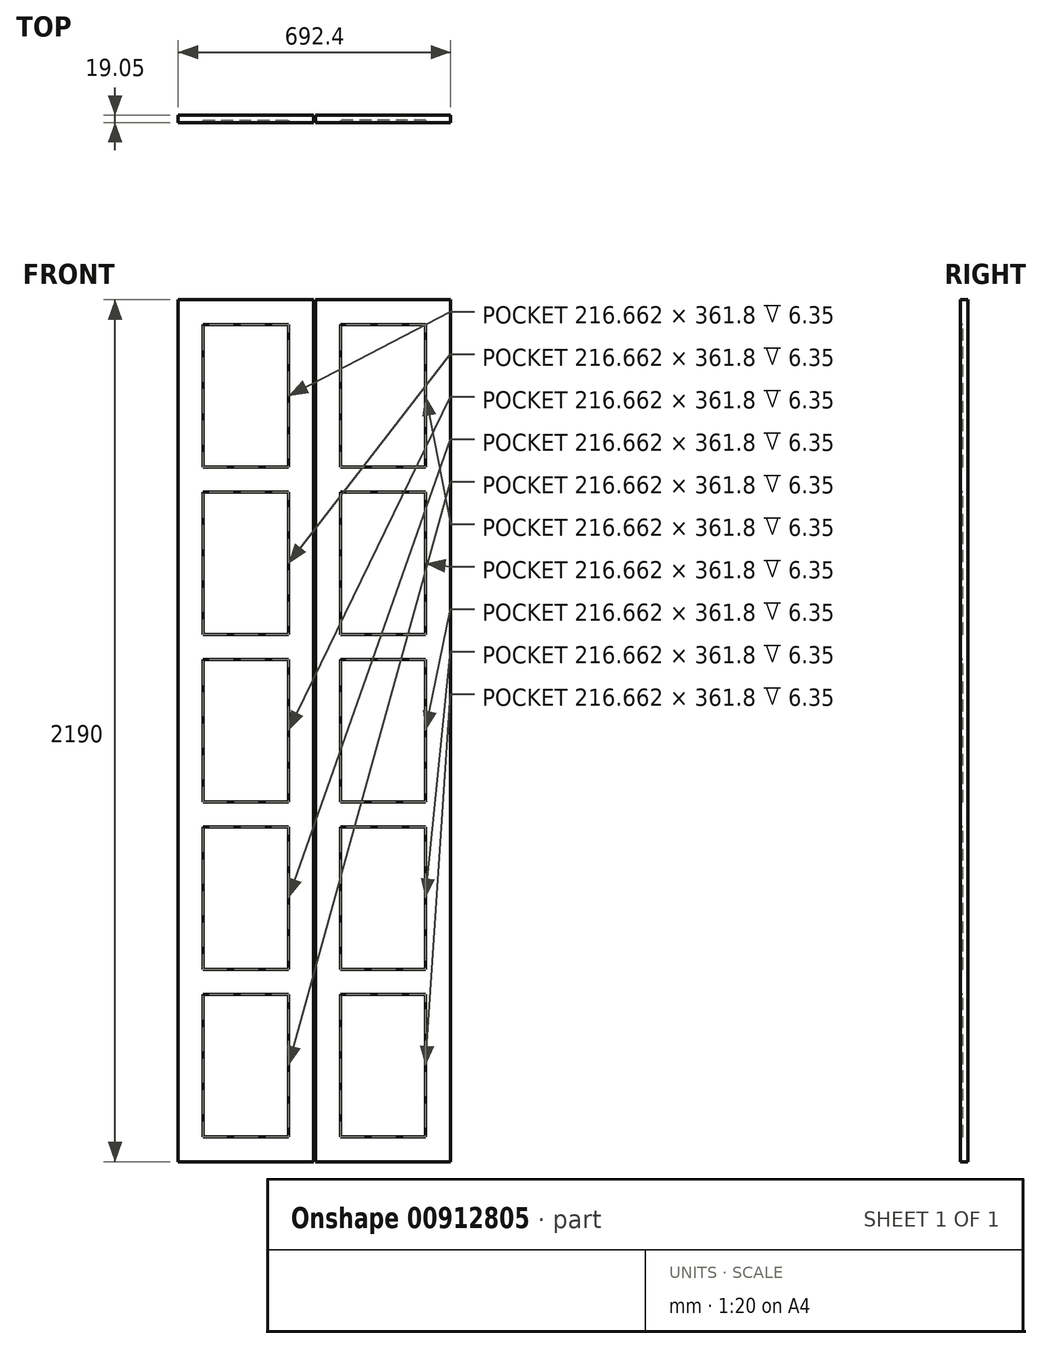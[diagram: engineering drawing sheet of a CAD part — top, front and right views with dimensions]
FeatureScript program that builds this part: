
annotation { "Feature Type Name" : "Feature", "Feature Type Description" : "" }
export const myFeature = defineFeature(function(context is Context, id is Id, definition is map)
    precondition{}
    {
        {
            var Q0;
            Q0=qCreatedBy(makeId("Front.planeOp"),FACE);
            var sketch = newSketch(context, id + "F0", { "sketchPlane" : qUnion([Q0])});
            skLineSegment(sketch, "E0.bottom", {"start": v(-336.55, 0) * mm, "end": v(336.55, 0) * mm, "construction": true});
            skLineSegment(sketch, "E0.top", {"start": v(-336.55, 2159) * mm, "end": v(336.55, 2159) * mm, "construction": true});
            skLineSegment(sketch, "E0.left", {"start": v(-336.55, 0) * mm, "end": v(-336.55, 2159) * mm, "construction": true});
            skLineSegment(sketch, "E0.right", {"start": v(336.55, 0) * mm, "end": v(336.55, 2159) * mm, "construction": true});
            skLineSegment(sketch, "E1.bottom", {"start": v(-336.55, 1814) * mm, "end": v(336.55, 1814) * mm, "construction": true});
            skLineSegment(sketch, "E1.top", {"start": v(-336.55, 1795) * mm, "end": v(336.55, 1795) * mm, "construction": true});
            skLineSegment(sketch, "E1.left", {"start": v(-336.55, 1814) * mm, "end": v(-336.55, 1795) * mm, "construction": true});
            skLineSegment(sketch, "E1.right", {"start": v(336.55, 1814) * mm, "end": v(336.55, 1795) * mm, "construction": true});
            skLineSegment(sketch, "E2.bottom", {"start": v(-336.55, 1450) * mm, "end": v(336.55, 1450) * mm, "construction": true});
            skLineSegment(sketch, "E2.top", {"start": v(-336.55, 1431) * mm, "end": v(336.55, 1431) * mm, "construction": true});
            skLineSegment(sketch, "E2.left", {"start": v(-336.55, 1450) * mm, "end": v(-336.55, 1431) * mm, "construction": true});
            skLineSegment(sketch, "E2.right", {"start": v(336.55, 1450) * mm, "end": v(336.55, 1431) * mm, "construction": true});
            skLineSegment(sketch, "E3.bottom", {"start": v(-336.55, 1086) * mm, "end": v(336.55, 1086) * mm, "construction": true});
            skLineSegment(sketch, "E3.top", {"start": v(-336.55, 1067) * mm, "end": v(336.55, 1067) * mm, "construction": true});
            skLineSegment(sketch, "E3.left", {"start": v(-336.55, 1086) * mm, "end": v(-336.55, 1067) * mm, "construction": true});
            skLineSegment(sketch, "E3.right", {"start": v(336.55, 1086) * mm, "end": v(336.55, 1067) * mm, "construction": true});
            skLineSegment(sketch, "E4.bottom", {"start": v(-336.55, 722) * mm, "end": v(336.55, 722) * mm, "construction": true});
            skLineSegment(sketch, "E4.top", {"start": v(-336.55, 703) * mm, "end": v(336.55, 703) * mm, "construction": true});
            skLineSegment(sketch, "E4.left", {"start": v(-336.55, 722) * mm, "end": v(-336.55, 703) * mm, "construction": true});
            skLineSegment(sketch, "E4.right", {"start": v(336.55, 722) * mm, "end": v(336.55, 703) * mm, "construction": true});
            skLineSegment(sketch, "E5.bottom", {"start": v(-336.55, 358) * mm, "end": v(336.55, 358) * mm, "construction": true});
            skLineSegment(sketch, "E5.top", {"start": v(-336.55, 339) * mm, "end": v(336.55, 339) * mm, "construction": true});
            skLineSegment(sketch, "E5.left", {"start": v(-336.55, 358) * mm, "end": v(-336.55, 339) * mm, "construction": true});
            skLineSegment(sketch, "E5.right", {"start": v(336.55, 358) * mm, "end": v(336.55, 339) * mm, "construction": true});
            skLineSegment(sketch, "E6.bottom", {"start": v(-336.55, 2079) * mm, "end": v(-246.69, 2079) * mm, "construction": true});
            skLineSegment(sketch, "E6.top", {"start": v(-336.55, 2019) * mm, "end": v(-246.69, 2019) * mm, "construction": true});
            skLineSegment(sketch, "E6.left", {"start": v(-336.55, 2079) * mm, "end": v(-336.55, 2019) * mm, "construction": true});
            skLineSegment(sketch, "E6.right", {"start": v(-246.69, 2079) * mm, "end": v(-246.69, 2019) * mm, "construction": true});
            skLineSegment(sketch, "E7.bottom", {"start": v(-336.55, 140) * mm, "end": v(-226.27, 140) * mm, "construction": true});
            skLineSegment(sketch, "E7.top", {"start": v(-336.55, 80) * mm, "end": v(-226.27, 80) * mm, "construction": true});
            skLineSegment(sketch, "E7.left", {"start": v(-336.55, 140) * mm, "end": v(-336.55, 80) * mm, "construction": true});
            skLineSegment(sketch, "E7.right", {"start": v(-226.27, 140) * mm, "end": v(-226.27, 80) * mm, "construction": true});
            skLineSegment(sketch, "E8.bottom", {"start": v(-336.55, 800) * mm, "end": v(-223.16, 800) * mm, "construction": true});
            skLineSegment(sketch, "E8.top", {"start": v(-336.55, 740) * mm, "end": v(-223.16, 740) * mm, "construction": true});
            skLineSegment(sketch, "E8.left", {"start": v(-336.55, 800) * mm, "end": v(-336.55, 740) * mm, "construction": true});
            skLineSegment(sketch, "E8.right", {"start": v(-223.16, 800) * mm, "end": v(-223.16, 740) * mm, "construction": true});
            skLineSegment(sketch, "E9.bottom", {"start": v(-336.55, 1419) * mm, "end": v(-246.69, 1419) * mm, "construction": true});
            skLineSegment(sketch, "E9.top", {"start": v(-336.55, 1359) * mm, "end": v(-246.69, 1359) * mm, "construction": true});
            skLineSegment(sketch, "E9.left", {"start": v(-336.55, 1419) * mm, "end": v(-336.55, 1359) * mm, "construction": true});
            skLineSegment(sketch, "E9.right", {"start": v(-246.69, 1419) * mm, "end": v(-246.69, 1359) * mm, "construction": true});
            skLineSegment(sketch, "E10", {"start": v(-330.44, 2169) * mm, "end": v(-118.46, 2169) * mm, "construction": true});
            skLineSegment(sketch, "E11", {"start": v(-246.69, 2049) * mm, "end": v(-304.11, 2049) * mm, "construction": true});
            skLineSegment(sketch, "E12", {"start": v(-246.69, 1389) * mm, "end": v(-303.87, 1389) * mm, "construction": true});
            skLineSegment(sketch, "E13", {"start": v(-223.16, 770) * mm, "end": v(-296.62, 770) * mm, "construction": true});
            skLineSegment(sketch, "E14", {"start": v(-226.27, 110) * mm, "end": v(-290.27, 110) * mm, "construction": true});
            skSolve(sketch);
        }
        {
            var Q0;
            Q0=qCreatedBy(makeId("Front.planeOp"),FACE);
            var sketch = newSketch(context, id + "F1", { "sketchPlane" : qUnion([Q0])});
            skLineSegment(sketch, "E15.bottom", {"start": v(-346.2, -21.35) * mm, "end": v(-2.54, -21.35) * mm});
            skLineSegment(sketch, "E15.top", {"start": v(-346.2, 2168.65) * mm, "end": v(-2.54, 2168.65) * mm});
            skLineSegment(sketch, "E15.left", {"start": v(-346.2, -21.35) * mm, "end": v(-346.2, 2168.65) * mm});
            skLineSegment(sketch, "E15.right", {"start": v(-2.54, -21.35) * mm, "end": v(-2.54, 2168.65) * mm});
            skSolve(sketch);
        }
        {
            var Q0;
            Q0 = qSketchRegion(id + "F1", true);
            extrude(context, id + "F2", {"entities" : qUnion([Q0]), "depth" : 19.05 * mm, "offsetDistance" : 25.4 * mm});
        }
        {
            var Q0;
            Q0=makeQuery(id+"F2.opExtrude","CAP_FACE",FACE,{"disambiguationData":[OSD([sQuery(id+"F1.wireOp",EDGE,"E15.bottom"),sQuery(id+"F1.wireOp",EDGE,"E15.top"),sQuery(id+"F1.wireOp",EDGE,"E15.left"),sQuery(id+"F1.wireOp",EDGE,"E15.right")])],"isStart":false});
            var sketch = newSketch(context, id + "F3", { "sketchPlane" : qUnion([Q0])});
            skLineSegment(sketch, "E16.bottom", {"start": v(-282.7, 42.15) * mm, "end": v(-66.04, 42.15) * mm});
            skLineSegment(sketch, "E16.top", {"start": v(-282.7, 403.95) * mm, "end": v(-66.04, 403.95) * mm});
            skLineSegment(sketch, "E16.left", {"start": v(-282.7, 42.15) * mm, "end": v(-282.7, 403.95) * mm});
            skLineSegment(sketch, "E16.right", {"start": v(-66.04, 42.15) * mm, "end": v(-66.04, 403.95) * mm});
            skLineSegment(sketch, "E17.bottom", {"start": v(-282.7, 467.45) * mm, "end": v(-66.04, 467.45) * mm});
            skLineSegment(sketch, "E17.top", {"start": v(-282.7, 829.25) * mm, "end": v(-66.04, 829.25) * mm});
            skLineSegment(sketch, "E17.left", {"start": v(-282.7, 467.45) * mm, "end": v(-282.7, 829.25) * mm});
            skLineSegment(sketch, "E17.right", {"start": v(-66.04, 467.45) * mm, "end": v(-66.04, 829.25) * mm});
            skLineSegment(sketch, "E18.bottom", {"start": v(-282.7, 892.75) * mm, "end": v(-66.04, 892.75) * mm});
            skLineSegment(sketch, "E18.top", {"start": v(-282.7, 1254.55) * mm, "end": v(-66.04, 1254.55) * mm});
            skLineSegment(sketch, "E18.left", {"start": v(-282.7, 892.75) * mm, "end": v(-282.7, 1254.55) * mm});
            skLineSegment(sketch, "E18.right", {"start": v(-66.04, 892.75) * mm, "end": v(-66.04, 1254.55) * mm});
            skLineSegment(sketch, "E19.bottom", {"start": v(-282.7, 1318.05) * mm, "end": v(-66.04, 1318.05) * mm});
            skLineSegment(sketch, "E19.top", {"start": v(-282.7, 1679.85) * mm, "end": v(-66.04, 1679.85) * mm});
            skLineSegment(sketch, "E19.left", {"start": v(-282.7, 1318.05) * mm, "end": v(-282.7, 1679.85) * mm});
            skLineSegment(sketch, "E19.right", {"start": v(-66.04, 1318.05) * mm, "end": v(-66.04, 1679.85) * mm});
            skLineSegment(sketch, "E20.bottom", {"start": v(-282.7, 1743.35) * mm, "end": v(-66.04, 1743.35) * mm});
            skLineSegment(sketch, "E20.top", {"start": v(-282.7, 2105.15) * mm, "end": v(-66.04, 2105.15) * mm});
            skLineSegment(sketch, "E20.left", {"start": v(-282.7, 1743.35) * mm, "end": v(-282.7, 2105.15) * mm});
            skLineSegment(sketch, "E20.right", {"start": v(-66.04, 1743.35) * mm, "end": v(-66.04, 2105.15) * mm});
            skSolve(sketch);
        }
        {
            var Q0;
            Q0 = qSketchRegion(id + "F3", true);
            extrude(context, id + "F4", {"entities" : qUnion([Q0]), "operationType" : NewBodyOperationType.REMOVE, "oppositeDirection" : true, "depth" : 6.35 * mm, "offsetDistance" : 25.4 * mm});
        }
        {
            var Q0;
            Q0=makeQuery(id+"F2.opExtrude","SWEPT_BODY",BODY,{"disambiguationData":[OSD([sQuery(id+"F1.wireOp",EDGE,"E15.bottom"),sQuery(id+"F1.wireOp",EDGE,"E15.top"),sQuery(id+"F1.wireOp",EDGE,"E15.left"),sQuery(id+"F1.wireOp",EDGE,"E15.right")])]});
            var Q1;
            Q1=qCreatedBy(makeId("Right.planeOp"),FACE);
            mirror(context, id + "F5", {"entities" : qUnion([Q0]), "mirrorPlane" : qUnion([Q1])});
        }
    });
